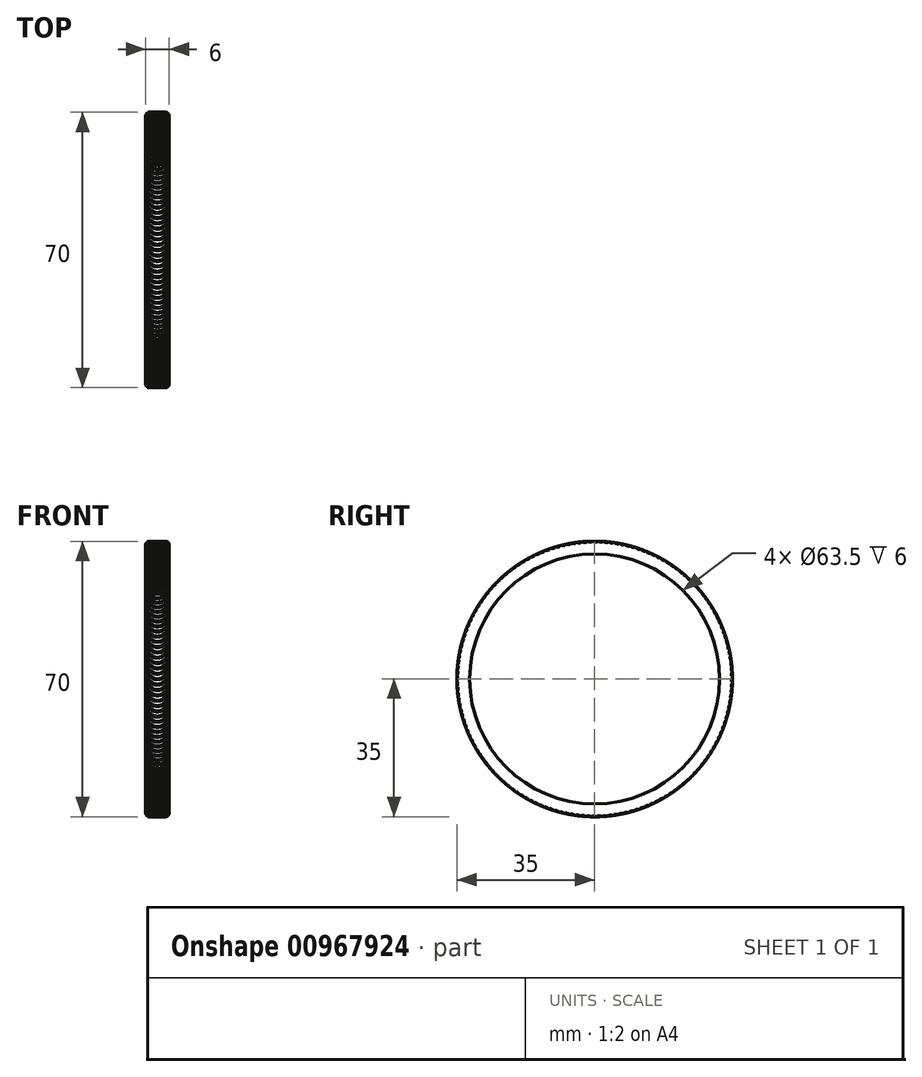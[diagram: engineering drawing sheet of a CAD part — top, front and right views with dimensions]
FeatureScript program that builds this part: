
annotation { "Feature Type Name" : "Feature", "Feature Type Description" : "" }
export const myFeature = defineFeature(function(context is Context, id is Id, definition is map)
    precondition{}
    {
        {
            var Q0;
            Q0=qCreatedBy(makeId("Right.planeOp"),FACE);
            var sketch = newSketch(context, id + "F0", { "sketchPlane" : qUnion([Q0])});
            skCircle(sketch, "E0", {"center": v(0, 0) * mm, "radius": 35 * mm});
            skCircle(sketch, "E1", {"center": v(0, 0) * mm, "radius": 31.75 * mm});
            skSolve(sketch);
        }
        {
            var Q0;
            Q0=makeQuery(id+"F0.imprint","IMPRINT",FACE,{"disambiguationData":[TD([[makeQuery(id+"F0.imprint","IMPRINT",EDGE,{"derivedFrom":sQuery(id+"F0.wireOp",EDGE,"E0")}),1.0]])]});
            extrude(context, id + "F1", {"entities" : qUnion([Q0]), "depth" : 6 * mm, "offsetDistance" : 25 * mm, "symmetric" : true});
        }
        {
            var Q0;
            Q0=makeQuery(id+"F1.opExtrude","CAP_EDGE",EDGE,{"disambiguationData":[OSD([sQuery(id+"F0.wireOp",EDGE,"E0")])],"isStart":false});
            var Q1;
            Q1=makeQuery(id+"F1.opExtrude","CAP_EDGE",EDGE,{"disambiguationData":[OSD([sQuery(id+"F0.wireOp",EDGE,"E0")])],"isStart":true});
            fillet(context, id + "F2", {"entities" : qUnion([Q0, Q1]), "radius" : 1 * mm, "tangentPropagation" : true, "allowEdgeOverflow" : false});
        }
        {
            var Q0;
            Q0=qCreatedBy(makeId("Front.planeOp"),FACE);
            var sketch = newSketch(context, id + "F3", { "sketchPlane" : qUnion([Q0])});
            skArc(sketch, "E2", {"start": v(-2.9, 0) * mm, "mid": v(0, -2.9) * mm, "end": v(2.9, 0) * mm});
            skArc(sketch, "E3", {"start": v(-2.7, 0) * mm, "mid": v(0, -2.7) * mm, "end": v(2.7, 0) * mm});
            skLineSegment(sketch, "E4", {"start": v(2.9, 0) * mm, "end": v(-2.9, 0) * mm});
            skSolve(sketch);
        }
        {
            var Q0;
            {var subQ0=sQuery(id+"F3.wireOp",EDGE,"E2");Q0=makeQuery(id+"F3.imprint","IMPRINT",FACE,{"disambiguationData":[TD([[makeQuery(id+"F3.imprint","IMPRINT",EDGE,{"derivedFrom":subQ0}),1.0]])]});}
            extrude(context, id + "F4", {"entities" : qUnion([Q0]), "depth" : 50.2 * mm, "offsetDistance" : 25 * mm, "hasSecondDirection" : true, "secondDirectionOppositeDirection" : false, "secondDirectionDepth" : 34.8 * mm});
        }
        {
            var Q0;
            Q0=makeQuery(id+"F4.opExtrude","SWEPT_BODY",BODY,{"disambiguationData":[OSD([sQuery(id+"F3.wireOp",EDGE,"E2"),sQuery(id+"F3.wireOp",EDGE,"E3"),sQuery(id+"F3.wireOp",EDGE,"E4")])]});
            var Q1;
            Q1=sQuery(id+"F3.wireOp",EDGE,"E4");
            circularPattern(context, id + "F5", {"operationType" : NewBodyOperationType.REMOVE, "entities" : qUnion([Q0]), "axis" : qUnion([Q1]), "angle" : 360 * degree, "instanceCount" : 160, "equalSpace" : true});
        }
    });
